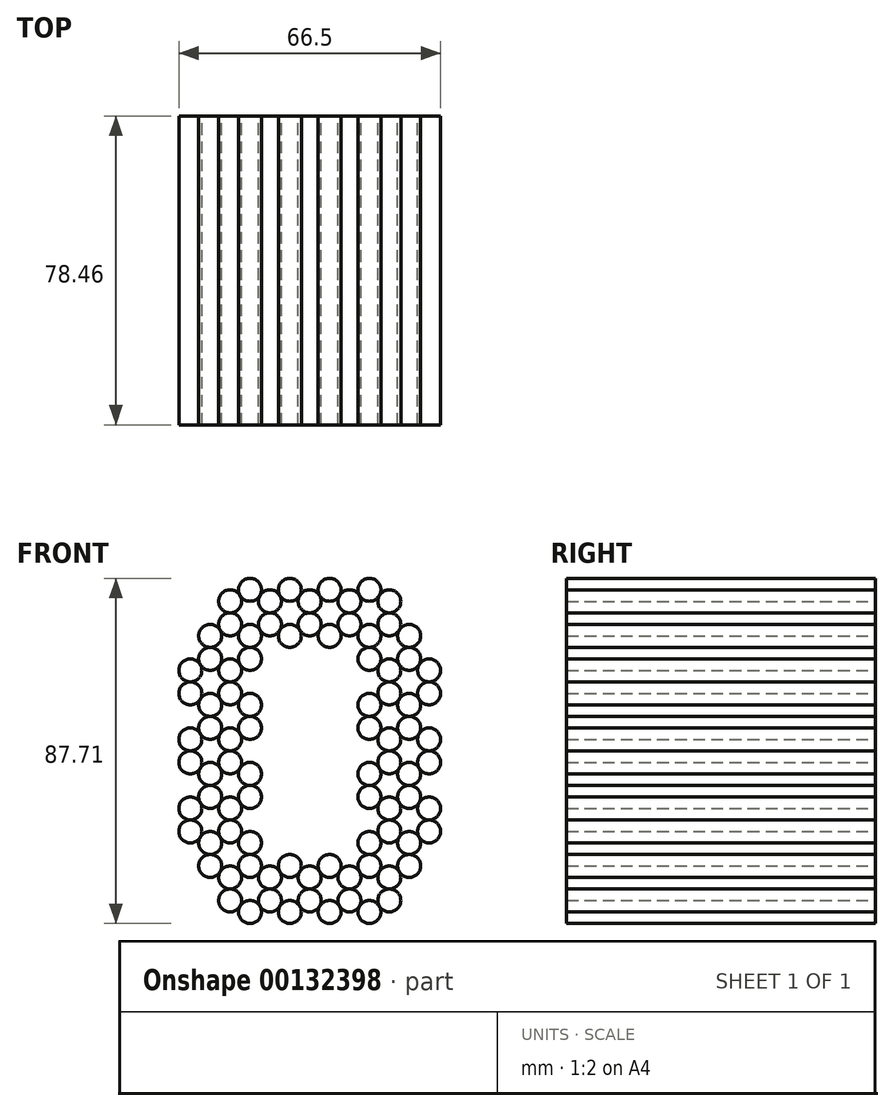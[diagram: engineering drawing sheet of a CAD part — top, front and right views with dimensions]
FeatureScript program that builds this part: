
annotation { "Feature Type Name" : "Feature", "Feature Type Description" : "" }
export const myFeature = defineFeature(function(context is Context, id is Id, definition is map)
    precondition{}
    {
        {
            var Q0;
            Q0=qCreatedBy(makeId("Front.planeOp"),FACE);
            var sketch = newSketch(context, id + "F0", { "sketchPlane" : qUnion([Q0])});
            skCircle(sketch, "E0", {"center": v(0, 0) * mm, "radius": 2.92 * mm});
            skCircle(sketch, "E1", {"center": v(5.05, 8.77) * mm, "radius": 2.92 * mm});
            skCircle(sketch, "E2", {"center": v(5.05, -2.93) * mm, "radius": 2.92 * mm});
            skCircle(sketch, "E3", {"center": v(10.1, 0) * mm, "radius": 2.92 * mm});
            skCircle(sketch, "E4", {"center": v(15.16, -2.93) * mm, "radius": 2.92 * mm});
            skCircle(sketch, "E5", {"center": v(10.1, 5.84) * mm, "radius": 2.92 * mm});
            skCircle(sketch, "E6", {"center": v(20.22, 0) * mm, "radius": 2.92 * mm});
            skCircle(sketch, "E7", {"center": v(20.22, 5.84) * mm, "radius": 2.92 * mm});
            skCircle(sketch, "E8", {"center": v(15.16, 8.77) * mm, "radius": 2.92 * mm});
            skCircle(sketch, "E9", {"center": v(-5.05, -2.93) * mm, "radius": 2.92 * mm});
            skCircle(sketch, "E10", {"center": v(0, 5.84) * mm, "radius": 2.92 * mm});
            skCircle(sketch, "E11", {"center": v(-5.05, 8.77) * mm, "radius": 2.92 * mm});
            skCircle(sketch, "E12", {"center": v(-10.1, 0) * mm, "radius": 2.92 * mm});
            skCircle(sketch, "E13", {"center": v(-15.16, 8.77) * mm, "radius": 2.92 * mm});
            skCircle(sketch, "E14", {"center": v(-10.1, 5.84) * mm, "radius": 2.92 * mm});
            skCircle(sketch, "E15", {"center": v(-20.22, 5.84) * mm, "radius": 2.92 * mm});
            skCircle(sketch, "E16", {"center": v(-20.22, 0) * mm, "radius": 2.92 * mm});
            skCircle(sketch, "E17", {"center": v(-15.16, -2.93) * mm, "radius": 2.92 * mm});
            skCircle(sketch, "E18", {"center": v(-25.27, -2.93) * mm, "radius": 2.92 * mm});
            skCircle(sketch, "E19", {"center": v(-25.27, -8.77) * mm, "radius": 2.92 * mm});
            skCircle(sketch, "E20", {"center": v(-20.22, -11.7) * mm, "radius": 2.92 * mm});
            skCircle(sketch, "E21", {"center": v(-15.16, -8.77) * mm, "radius": 2.92 * mm});
            skCircle(sketch, "E22", {"center": v(-30.33, -11.7) * mm, "radius": 2.92 * mm});
            skCircle(sketch, "E23", {"center": v(-30.33, -17.54) * mm, "radius": 2.92 * mm});
            skCircle(sketch, "E24", {"center": v(-25.27, -20.47) * mm, "radius": 2.92 * mm});
            skCircle(sketch, "E25", {"center": v(-20.22, -17.54) * mm, "radius": 2.92 * mm});
            skCircle(sketch, "E26", {"center": v(-15.16, -20.47) * mm, "radius": 2.92 * mm});
            skCircle(sketch, "E27", {"center": v(-25.27, -26.31) * mm, "radius": 2.92 * mm});
            skCircle(sketch, "E28", {"center": v(-20.22, -29.24) * mm, "radius": 2.92 * mm});
            skCircle(sketch, "E29", {"center": v(-15.16, -26.31) * mm, "radius": 2.92 * mm});
            skCircle(sketch, "E30", {"center": v(-30.33, -29.24) * mm, "radius": 2.92 * mm});
            skCircle(sketch, "E31", {"center": v(-30.33, -35.08) * mm, "radius": 2.92 * mm});
            skCircle(sketch, "E32", {"center": v(-25.27, -38.01) * mm, "radius": 2.92 * mm});
            skCircle(sketch, "E33", {"center": v(-20.22, -35.08) * mm, "radius": 2.92 * mm});
            skCircle(sketch, "E34", {"center": v(-15.16, -38.01) * mm, "radius": 2.92 * mm});
            skCircle(sketch, "E35", {"center": v(-25.27, -43.86) * mm, "radius": 2.92 * mm});
            skCircle(sketch, "E36", {"center": v(-20.22, -46.78) * mm, "radius": 2.92 * mm});
            skCircle(sketch, "E37", {"center": v(-15.16, -43.86) * mm, "radius": 2.92 * mm});
            skCircle(sketch, "E38", {"center": v(-30.33, -46.78) * mm, "radius": 2.92 * mm});
            skCircle(sketch, "E39", {"center": v(-30.33, -52.63) * mm, "radius": 2.92 * mm});
            skCircle(sketch, "E40", {"center": v(-25.27, -55.56) * mm, "radius": 2.92 * mm});
            skCircle(sketch, "E41", {"center": v(-20.22, -52.63) * mm, "radius": 2.92 * mm});
            skCircle(sketch, "E42", {"center": v(-15.16, -55.56) * mm, "radius": 2.92 * mm});
            skCircle(sketch, "E43", {"center": v(-25.27, -61.4) * mm, "radius": 2.92 * mm});
            skCircle(sketch, "E44", {"center": v(-20.22, -64.33) * mm, "radius": 2.92 * mm});
            skCircle(sketch, "E45", {"center": v(-15.16, -61.4) * mm, "radius": 2.92 * mm});
            skCircle(sketch, "E46", {"center": v(0, -70.17) * mm, "radius": 2.92 * mm});
            skCircle(sketch, "E47", {"center": v(5.05, -61.4) * mm, "radius": 2.92 * mm});
            skCircle(sketch, "E48", {"center": v(5.05, -73.1) * mm, "radius": 2.92 * mm});
            skCircle(sketch, "E49", {"center": v(10.1, -70.17) * mm, "radius": 2.92 * mm});
            skCircle(sketch, "E50", {"center": v(15.16, -73.1) * mm, "radius": 2.92 * mm});
            skCircle(sketch, "E51", {"center": v(10.1, -64.33) * mm, "radius": 2.92 * mm});
            skCircle(sketch, "E52", {"center": v(20.22, -70.17) * mm, "radius": 2.92 * mm});
            skCircle(sketch, "E53", {"center": v(20.22, -64.33) * mm, "radius": 2.92 * mm});
            skCircle(sketch, "E54", {"center": v(15.16, -61.4) * mm, "radius": 2.92 * mm});
            skCircle(sketch, "E55", {"center": v(-5.05, -73.1) * mm, "radius": 2.92 * mm});
            skCircle(sketch, "E56", {"center": v(0, -64.33) * mm, "radius": 2.92 * mm});
            skCircle(sketch, "E57", {"center": v(-5.05, -61.4) * mm, "radius": 2.92 * mm});
            skCircle(sketch, "E58", {"center": v(-10.1, -70.17) * mm, "radius": 2.92 * mm});
            skCircle(sketch, "E59", {"center": v(-10.1, -64.33) * mm, "radius": 2.92 * mm});
            skCircle(sketch, "E60", {"center": v(-20.22, -70.17) * mm, "radius": 2.92 * mm});
            skCircle(sketch, "E61", {"center": v(-15.16, -73.1) * mm, "radius": 2.92 * mm});
            skCircle(sketch, "E62", {"center": v(25.27, -20.47) * mm, "radius": 2.92 * mm});
            skCircle(sketch, "E63", {"center": v(15.16, -20.47) * mm, "radius": 2.92 * mm});
            skCircle(sketch, "E64", {"center": v(15.16, -26.31) * mm, "radius": 2.92 * mm});
            skCircle(sketch, "E65", {"center": v(20.22, -29.24) * mm, "radius": 2.92 * mm});
            skCircle(sketch, "E66", {"center": v(25.27, -26.31) * mm, "radius": 2.92 * mm});
            skCircle(sketch, "E67", {"center": v(30.33, -29.24) * mm, "radius": 2.92 * mm});
            skCircle(sketch, "E68", {"center": v(20.22, -35.08) * mm, "radius": 2.92 * mm});
            skCircle(sketch, "E69", {"center": v(25.27, -38.01) * mm, "radius": 2.92 * mm});
            skCircle(sketch, "E70", {"center": v(30.33, -35.08) * mm, "radius": 2.92 * mm});
            skCircle(sketch, "E71", {"center": v(15.16, -38.01) * mm, "radius": 2.92 * mm});
            skCircle(sketch, "E72", {"center": v(15.16, -43.86) * mm, "radius": 2.92 * mm});
            skCircle(sketch, "E73", {"center": v(20.22, -46.78) * mm, "radius": 2.92 * mm});
            skCircle(sketch, "E74", {"center": v(25.27, -43.86) * mm, "radius": 2.92 * mm});
            skCircle(sketch, "E75", {"center": v(30.33, -46.78) * mm, "radius": 2.92 * mm});
            skCircle(sketch, "E76", {"center": v(20.22, -52.63) * mm, "radius": 2.92 * mm});
            skCircle(sketch, "E77", {"center": v(25.27, -55.56) * mm, "radius": 2.92 * mm});
            skCircle(sketch, "E78", {"center": v(30.33, -52.63) * mm, "radius": 2.92 * mm});
            skCircle(sketch, "E79", {"center": v(15.16, -55.56) * mm, "radius": 2.92 * mm});
            skCircle(sketch, "E80", {"center": v(25.27, -61.4) * mm, "radius": 2.92 * mm});
            skCircle(sketch, "E81", {"center": v(15.16, -8.77) * mm, "radius": 2.92 * mm});
            skCircle(sketch, "E82", {"center": v(20.22, -17.54) * mm, "radius": 2.92 * mm});
            skCircle(sketch, "E83", {"center": v(20.22, -11.7) * mm, "radius": 2.92 * mm});
            skCircle(sketch, "E84", {"center": v(25.27, -2.93) * mm, "radius": 2.92 * mm});
            skCircle(sketch, "E85", {"center": v(25.27, -8.77) * mm, "radius": 2.92 * mm});
            skCircle(sketch, "E86", {"center": v(30.33, -17.54) * mm, "radius": 2.92 * mm});
            skCircle(sketch, "E87", {"center": v(30.33, -11.7) * mm, "radius": 2.92 * mm});
            skSolve(sketch);
        }
        {
            var Q0;
            {var subQ0=sQuery(id+"F0.wireOp",EDGE,"E69");var subQ1=makeQuery(id+"F0.imprint","INTERSECT",VERTEX,{"derivedFrom":[subQ0,sQuery(id+"F0.wireOp",EDGE,"E70")]});Q0=makeQuery(id+"F0.imprint","IMPRINT",FACE,{"disambiguationData":[TD([[makeQuery(id+"F0.imprint","IMPRINT",EDGE,{"disambiguationData":[TD([[subQ1,-1.0]])],"derivedFrom":subQ0}),1.0]])]});}
            var Q1;
            {var subQ0=sQuery(id+"F0.wireOp",EDGE,"E34");var subQ1=makeQuery(id+"F0.imprint","INTERSECT",VERTEX,{"derivedFrom":[sQuery(id+"F0.wireOp",EDGE,"E33"),subQ0]});Q1=makeQuery(id+"F0.imprint","IMPRINT",FACE,{"disambiguationData":[TD([[makeQuery(id+"F0.imprint","IMPRINT",EDGE,{"disambiguationData":[TD([[subQ1,-1.0]])],"derivedFrom":subQ0}),1.0]])]});}
            var Q2;
            {var subQ0=sQuery(id+"F0.wireOp",EDGE,"E86");var subQ1=makeQuery(id+"F0.imprint","INTERSECT",VERTEX,{"derivedFrom":[sQuery(id+"F0.wireOp",EDGE,"E62"),subQ0]});Q2=makeQuery(id+"F0.imprint","IMPRINT",FACE,{"disambiguationData":[TD([[makeQuery(id+"F0.imprint","IMPRINT",EDGE,{"disambiguationData":[TD([[subQ1,1.0]])],"derivedFrom":subQ0}),1.0]])]});}
            var Q3;
            {var subQ0=sQuery(id+"F0.wireOp",EDGE,"E33");var subQ1=makeQuery(id+"F0.imprint","INTERSECT",VERTEX,{"derivedFrom":[sQuery(id+"F0.wireOp",EDGE,"E28"),subQ0]});Q3=makeQuery(id+"F0.imprint","IMPRINT",FACE,{"disambiguationData":[TD([[makeQuery(id+"F0.imprint","IMPRINT",EDGE,{"disambiguationData":[TD([[subQ1,-1.0]])],"derivedFrom":subQ0}),1.0]])]});}
            var Q4;
            {var subQ0=sQuery(id+"F0.wireOp",EDGE,"E45");var subQ1=makeQuery(id+"F0.imprint","INTERSECT",VERTEX,{"derivedFrom":[sQuery(id+"F0.wireOp",EDGE,"E42"),subQ0]});Q4=makeQuery(id+"F0.imprint","IMPRINT",FACE,{"disambiguationData":[TD([[makeQuery(id+"F0.imprint","IMPRINT",EDGE,{"disambiguationData":[TD([[subQ1,-1.0]])],"derivedFrom":subQ0}),1.0]])]});}
            var Q5;
            {var subQ0=sQuery(id+"F0.wireOp",EDGE,"E74");var subQ1=makeQuery(id+"F0.imprint","INTERSECT",VERTEX,{"derivedFrom":[sQuery(id+"F0.wireOp",EDGE,"E69"),subQ0]});Q5=makeQuery(id+"F0.imprint","IMPRINT",FACE,{"disambiguationData":[TD([[makeQuery(id+"F0.imprint","IMPRINT",EDGE,{"disambiguationData":[TD([[subQ1,-1.0]])],"derivedFrom":subQ0}),1.0]])]});}
            var Q6;
            {var subQ0=sQuery(id+"F0.wireOp",EDGE,"E40");var subQ1=makeQuery(id+"F0.imprint","INTERSECT",VERTEX,{"derivedFrom":[sQuery(id+"F0.wireOp",EDGE,"E39"),subQ0]});Q6=makeQuery(id+"F0.imprint","IMPRINT",FACE,{"disambiguationData":[TD([[makeQuery(id+"F0.imprint","IMPRINT",EDGE,{"disambiguationData":[TD([[subQ1,1.0]])],"derivedFrom":subQ0}),1.0]])]});}
            var Q7;
            {var subQ0=sQuery(id+"F0.wireOp",EDGE,"E5");var subQ1=makeQuery(id+"F0.imprint","INTERSECT",VERTEX,{"derivedFrom":[sQuery(id+"F0.wireOp",EDGE,"E1"),subQ0]});Q7=makeQuery(id+"F0.imprint","IMPRINT",FACE,{"disambiguationData":[TD([[makeQuery(id+"F0.imprint","IMPRINT",EDGE,{"disambiguationData":[TD([[subQ1,1.0]])],"derivedFrom":subQ0}),1.0]])]});}
            var Q8;
            {var subQ0=sQuery(id+"F0.wireOp",EDGE,"E71");var subQ1=makeQuery(id+"F0.imprint","INTERSECT",VERTEX,{"derivedFrom":[sQuery(id+"F0.wireOp",EDGE,"E68"),subQ0]});Q8=makeQuery(id+"F0.imprint","IMPRINT",FACE,{"disambiguationData":[TD([[makeQuery(id+"F0.imprint","IMPRINT",EDGE,{"disambiguationData":[TD([[subQ1,-1.0]])],"derivedFrom":subQ0}),1.0]])]});}
            var Q9;
            {var subQ0=sQuery(id+"F0.wireOp",EDGE,"E35");var subQ1=makeQuery(id+"F0.imprint","INTERSECT",VERTEX,{"derivedFrom":[sQuery(id+"F0.wireOp",EDGE,"E32"),subQ0]});Q9=makeQuery(id+"F0.imprint","IMPRINT",FACE,{"disambiguationData":[TD([[makeQuery(id+"F0.imprint","IMPRINT",EDGE,{"disambiguationData":[TD([[subQ1,-1.0]])],"derivedFrom":subQ0}),1.0]])]});}
            var Q10;
            {var subQ0=sQuery(id+"F0.wireOp",EDGE,"E87");var subQ1=makeQuery(id+"F0.imprint","INTERSECT",VERTEX,{"derivedFrom":[sQuery(id+"F0.wireOp",EDGE,"E85"),subQ0]});Q10=makeQuery(id+"F0.imprint","IMPRINT",FACE,{"disambiguationData":[TD([[makeQuery(id+"F0.imprint","IMPRINT",EDGE,{"disambiguationData":[TD([[subQ1,-1.0]])],"derivedFrom":subQ0}),1.0]])]});}
            var Q11;
            {var subQ0=sQuery(id+"F0.wireOp",EDGE,"E36");var subQ1=makeQuery(id+"F0.imprint","INTERSECT",VERTEX,{"derivedFrom":[sQuery(id+"F0.wireOp",EDGE,"E35"),subQ0]});Q11=makeQuery(id+"F0.imprint","IMPRINT",FACE,{"disambiguationData":[TD([[makeQuery(id+"F0.imprint","IMPRINT",EDGE,{"disambiguationData":[TD([[subQ1,1.0]])],"derivedFrom":subQ0}),1.0]])]});}
            var Q12;
            {var subQ0=sQuery(id+"F0.wireOp",EDGE,"E51");var subQ1=makeQuery(id+"F0.imprint","INTERSECT",VERTEX,{"derivedFrom":[sQuery(id+"F0.wireOp",EDGE,"E47"),subQ0]});Q12=makeQuery(id+"F0.imprint","IMPRINT",FACE,{"disambiguationData":[TD([[makeQuery(id+"F0.imprint","IMPRINT",EDGE,{"disambiguationData":[TD([[subQ1,1.0]])],"derivedFrom":subQ0}),1.0]])]});}
            var Q13;
            {var subQ0=sQuery(id+"F0.wireOp",EDGE,"E77");var subQ1=makeQuery(id+"F0.imprint","INTERSECT",VERTEX,{"derivedFrom":[subQ0,sQuery(id+"F0.wireOp",EDGE,"E78")]});Q13=makeQuery(id+"F0.imprint","IMPRINT",FACE,{"disambiguationData":[TD([[makeQuery(id+"F0.imprint","IMPRINT",EDGE,{"disambiguationData":[TD([[subQ1,-1.0]])],"derivedFrom":subQ0}),1.0]])]});}
            var Q14;
            {var subQ0=sQuery(id+"F0.wireOp",EDGE,"E42");var subQ1=makeQuery(id+"F0.imprint","INTERSECT",VERTEX,{"derivedFrom":[sQuery(id+"F0.wireOp",EDGE,"E41"),subQ0]});Q14=makeQuery(id+"F0.imprint","IMPRINT",FACE,{"disambiguationData":[TD([[makeQuery(id+"F0.imprint","IMPRINT",EDGE,{"disambiguationData":[TD([[subQ1,-1.0]])],"derivedFrom":subQ0}),1.0]])]});}
            var Q15;
            {var subQ0=sQuery(id+"F0.wireOp",EDGE,"E6");var subQ1=makeQuery(id+"F0.imprint","INTERSECT",VERTEX,{"derivedFrom":[subQ0,sQuery(id+"F0.wireOp",EDGE,"E7")]});Q15=makeQuery(id+"F0.imprint","IMPRINT",FACE,{"disambiguationData":[TD([[makeQuery(id+"F0.imprint","IMPRINT",EDGE,{"disambiguationData":[TD([[subQ1,-1.0]])],"derivedFrom":subQ0}),1.0]])]});}
            var Q16;
            {var subQ0=sQuery(id+"F0.wireOp",EDGE,"E72");var subQ1=makeQuery(id+"F0.imprint","INTERSECT",VERTEX,{"derivedFrom":[sQuery(id+"F0.wireOp",EDGE,"E71"),subQ0]});Q16=makeQuery(id+"F0.imprint","IMPRINT",FACE,{"disambiguationData":[TD([[makeQuery(id+"F0.imprint","IMPRINT",EDGE,{"disambiguationData":[TD([[subQ1,-1.0]])],"derivedFrom":subQ0}),1.0]])]});}
            var Q17;
            {var subQ0=sQuery(id+"F0.wireOp",EDGE,"E37");var subQ1=makeQuery(id+"F0.imprint","INTERSECT",VERTEX,{"derivedFrom":[sQuery(id+"F0.wireOp",EDGE,"E34"),subQ0]});Q17=makeQuery(id+"F0.imprint","IMPRINT",FACE,{"disambiguationData":[TD([[makeQuery(id+"F0.imprint","IMPRINT",EDGE,{"disambiguationData":[TD([[subQ1,-1.0]])],"derivedFrom":subQ0}),1.0]])]});}
            var Q18;
            {var subQ0=sQuery(id+"F0.wireOp",EDGE,"E2");var subQ1=makeQuery(id+"F0.imprint","INTERSECT",VERTEX,{"derivedFrom":[sQuery(id+"F0.wireOp",EDGE,"E0"),subQ0]});Q18=makeQuery(id+"F0.imprint","IMPRINT",FACE,{"disambiguationData":[TD([[makeQuery(id+"F0.imprint","IMPRINT",EDGE,{"disambiguationData":[TD([[subQ1,1.0]])],"derivedFrom":subQ0}),1.0]])]});}
            var Q19;
            {var subQ0=sQuery(id+"F0.wireOp",EDGE,"E41");var subQ1=makeQuery(id+"F0.imprint","INTERSECT",VERTEX,{"derivedFrom":[sQuery(id+"F0.wireOp",EDGE,"E36"),subQ0]});Q19=makeQuery(id+"F0.imprint","IMPRINT",FACE,{"disambiguationData":[TD([[makeQuery(id+"F0.imprint","IMPRINT",EDGE,{"disambiguationData":[TD([[subQ1,-1.0]])],"derivedFrom":subQ0}),1.0]])]});}
            var Q20;
            {var subQ0=sQuery(id+"F0.wireOp",EDGE,"E52");var subQ1=makeQuery(id+"F0.imprint","INTERSECT",VERTEX,{"derivedFrom":[sQuery(id+"F0.wireOp",EDGE,"E50"),subQ0]});Q20=makeQuery(id+"F0.imprint","IMPRINT",FACE,{"disambiguationData":[TD([[makeQuery(id+"F0.imprint","IMPRINT",EDGE,{"disambiguationData":[TD([[subQ1,1.0]])],"derivedFrom":subQ0}),1.0]])]});}
            var Q21;
            {var subQ0=sQuery(id+"F0.wireOp",EDGE,"E56");var subQ1=makeQuery(id+"F0.imprint","INTERSECT",VERTEX,{"derivedFrom":[sQuery(id+"F0.wireOp",EDGE,"E46"),subQ0]});Q21=makeQuery(id+"F0.imprint","IMPRINT",FACE,{"disambiguationData":[TD([[makeQuery(id+"F0.imprint","IMPRINT",EDGE,{"disambiguationData":[TD([[subQ1,1.0]])],"derivedFrom":subQ0}),1.0]])]});}
            var Q22;
            {var subQ0=sQuery(id+"F0.wireOp",EDGE,"E81");var subQ1=makeQuery(id+"F0.imprint","INTERSECT",VERTEX,{"derivedFrom":[sQuery(id+"F0.wireOp",EDGE,"E4"),subQ0]});Q22=makeQuery(id+"F0.imprint","IMPRINT",FACE,{"disambiguationData":[TD([[makeQuery(id+"F0.imprint","IMPRINT",EDGE,{"disambiguationData":[TD([[subQ1,-1.0]])],"derivedFrom":subQ0}),1.0]])]});}
            var Q23;
            {var subQ0=sQuery(id+"F0.wireOp",EDGE,"E46");var subQ1=makeQuery(id+"F0.imprint","INTERSECT",VERTEX,{"derivedFrom":[subQ0,sQuery(id+"F0.wireOp",EDGE,"E55")]});Q23=makeQuery(id+"F0.imprint","IMPRINT",FACE,{"disambiguationData":[TD([[makeQuery(id+"F0.imprint","IMPRINT",EDGE,{"disambiguationData":[TD([[subQ1,1.0]])],"derivedFrom":subQ0}),1.0]])]});}
            var Q24;
            {var subQ0=sQuery(id+"F0.wireOp",EDGE,"E10");var subQ1=makeQuery(id+"F0.imprint","INTERSECT",VERTEX,{"derivedFrom":[subQ0,sQuery(id+"F0.wireOp",EDGE,"E11")]});Q24=makeQuery(id+"F0.imprint","IMPRINT",FACE,{"disambiguationData":[TD([[makeQuery(id+"F0.imprint","IMPRINT",EDGE,{"disambiguationData":[TD([[subQ1,-1.0]])],"derivedFrom":subQ0}),1.0]])]});}
            var Q25;
            {var subQ0=sQuery(id+"F0.wireOp",EDGE,"E55");var subQ1=makeQuery(id+"F0.imprint","INTERSECT",VERTEX,{"derivedFrom":[sQuery(id+"F0.wireOp",EDGE,"E46"),subQ0]});Q25=makeQuery(id+"F0.imprint","IMPRINT",FACE,{"disambiguationData":[TD([[makeQuery(id+"F0.imprint","IMPRINT",EDGE,{"disambiguationData":[TD([[subQ1,-1.0]])],"derivedFrom":subQ0}),1.0]])]});}
            var Q26;
            {var subQ0=sQuery(id+"F0.wireOp",EDGE,"E59");var subQ1=makeQuery(id+"F0.imprint","INTERSECT",VERTEX,{"derivedFrom":[sQuery(id+"F0.wireOp",EDGE,"E45"),subQ0]});Q26=makeQuery(id+"F0.imprint","IMPRINT",FACE,{"disambiguationData":[TD([[makeQuery(id+"F0.imprint","IMPRINT",EDGE,{"disambiguationData":[TD([[subQ1,1.0]])],"derivedFrom":subQ0}),1.0]])]});}
            var Q27;
            {var subQ0=sQuery(id+"F0.wireOp",EDGE,"E85");var subQ1=makeQuery(id+"F0.imprint","INTERSECT",VERTEX,{"derivedFrom":[sQuery(id+"F0.wireOp",EDGE,"E84"),subQ0]});Q27=makeQuery(id+"F0.imprint","IMPRINT",FACE,{"disambiguationData":[TD([[makeQuery(id+"F0.imprint","IMPRINT",EDGE,{"disambiguationData":[TD([[subQ1,-1.0]])],"derivedFrom":subQ0}),1.0]])]});}
            var Q28;
            {var subQ0=sQuery(id+"F0.wireOp",EDGE,"E47");var subQ1=makeQuery(id+"F0.imprint","INTERSECT",VERTEX,{"derivedFrom":[subQ0,sQuery(id+"F0.wireOp",EDGE,"E51")]});Q28=makeQuery(id+"F0.imprint","IMPRINT",FACE,{"disambiguationData":[TD([[makeQuery(id+"F0.imprint","IMPRINT",EDGE,{"disambiguationData":[TD([[subQ1,1.0]])],"derivedFrom":subQ0}),1.0]])]});}
            var Q29;
            {var subQ0=sQuery(id+"F0.wireOp",EDGE,"E14");var subQ1=makeQuery(id+"F0.imprint","INTERSECT",VERTEX,{"derivedFrom":[sQuery(id+"F0.wireOp",EDGE,"E11"),subQ0]});Q29=makeQuery(id+"F0.imprint","IMPRINT",FACE,{"disambiguationData":[TD([[makeQuery(id+"F0.imprint","IMPRINT",EDGE,{"disambiguationData":[TD([[subQ1,-1.0]])],"derivedFrom":subQ0}),1.0]])]});}
            var Q30;
            {var subQ0=sQuery(id+"F0.wireOp",EDGE,"E60");var subQ1=makeQuery(id+"F0.imprint","INTERSECT",VERTEX,{"derivedFrom":[sQuery(id+"F0.wireOp",EDGE,"E44"),subQ0]});Q30=makeQuery(id+"F0.imprint","IMPRINT",FACE,{"disambiguationData":[TD([[makeQuery(id+"F0.imprint","IMPRINT",EDGE,{"disambiguationData":[TD([[subQ1,-1.0]])],"derivedFrom":subQ0}),1.0]])]});}
            var Q31;
            {var subQ0=sQuery(id+"F0.wireOp",EDGE,"E65");var subQ1=makeQuery(id+"F0.imprint","INTERSECT",VERTEX,{"derivedFrom":[sQuery(id+"F0.wireOp",EDGE,"E64"),subQ0]});Q31=makeQuery(id+"F0.imprint","IMPRINT",FACE,{"disambiguationData":[TD([[makeQuery(id+"F0.imprint","IMPRINT",EDGE,{"disambiguationData":[TD([[subQ1,1.0]])],"derivedFrom":subQ0}),1.0]])]});}
            var Q32;
            {var subQ0=sQuery(id+"F0.wireOp",EDGE,"E0");var subQ1=makeQuery(id+"F0.imprint","INTERSECT",VERTEX,{"derivedFrom":[subQ0,sQuery(id+"F0.wireOp",EDGE,"E9")]});Q32=makeQuery(id+"F0.imprint","IMPRINT",FACE,{"disambiguationData":[TD([[makeQuery(id+"F0.imprint","IMPRINT",EDGE,{"disambiguationData":[TD([[subQ1,1.0]])],"derivedFrom":subQ0}),1.0]])]});}
            var Q33;
            {var subQ0=sQuery(id+"F0.wireOp",EDGE,"E49");var subQ1=makeQuery(id+"F0.imprint","INTERSECT",VERTEX,{"derivedFrom":[sQuery(id+"F0.wireOp",EDGE,"E48"),subQ0]});Q33=makeQuery(id+"F0.imprint","IMPRINT",FACE,{"disambiguationData":[TD([[makeQuery(id+"F0.imprint","IMPRINT",EDGE,{"disambiguationData":[TD([[subQ1,1.0]])],"derivedFrom":subQ0}),1.0]])]});}
            var Q34;
            {var subQ0=sQuery(id+"F0.wireOp",EDGE,"E16");var subQ1=makeQuery(id+"F0.imprint","INTERSECT",VERTEX,{"derivedFrom":[sQuery(id+"F0.wireOp",EDGE,"E15"),subQ0]});Q34=makeQuery(id+"F0.imprint","IMPRINT",FACE,{"disambiguationData":[TD([[makeQuery(id+"F0.imprint","IMPRINT",EDGE,{"disambiguationData":[TD([[subQ1,-1.0]])],"derivedFrom":subQ0}),1.0]])]});}
            var Q35;
            {var subQ0=sQuery(id+"F0.wireOp",EDGE,"E61");var subQ1=makeQuery(id+"F0.imprint","INTERSECT",VERTEX,{"derivedFrom":[sQuery(id+"F0.wireOp",EDGE,"E58"),subQ0]});Q35=makeQuery(id+"F0.imprint","IMPRINT",FACE,{"disambiguationData":[TD([[makeQuery(id+"F0.imprint","IMPRINT",EDGE,{"disambiguationData":[TD([[subQ1,-1.0]])],"derivedFrom":subQ0}),1.0]])]});}
            var Q36;
            {var subQ0=sQuery(id+"F0.wireOp",EDGE,"E68");var subQ1=makeQuery(id+"F0.imprint","INTERSECT",VERTEX,{"derivedFrom":[sQuery(id+"F0.wireOp",EDGE,"E65"),subQ0]});Q36=makeQuery(id+"F0.imprint","IMPRINT",FACE,{"disambiguationData":[TD([[makeQuery(id+"F0.imprint","IMPRINT",EDGE,{"disambiguationData":[TD([[subQ1,-1.0]])],"derivedFrom":subQ0}),1.0]])]});}
            var Q37;
            {var subQ0=sQuery(id+"F0.wireOp",EDGE,"E3");var subQ1=makeQuery(id+"F0.imprint","INTERSECT",VERTEX,{"derivedFrom":[sQuery(id+"F0.wireOp",EDGE,"E2"),subQ0]});Q37=makeQuery(id+"F0.imprint","IMPRINT",FACE,{"disambiguationData":[TD([[makeQuery(id+"F0.imprint","IMPRINT",EDGE,{"disambiguationData":[TD([[subQ1,1.0]])],"derivedFrom":subQ0}),1.0]])]});}
            var Q38;
            {var subQ0=sQuery(id+"F0.wireOp",EDGE,"E53");var subQ1=makeQuery(id+"F0.imprint","INTERSECT",VERTEX,{"derivedFrom":[subQ0,sQuery(id+"F0.wireOp",EDGE,"E80")]});Q38=makeQuery(id+"F0.imprint","IMPRINT",FACE,{"disambiguationData":[TD([[makeQuery(id+"F0.imprint","IMPRINT",EDGE,{"disambiguationData":[TD([[subQ1,-1.0]])],"derivedFrom":subQ0}),1.0]])]});}
            var Q39;
            {var subQ0=sQuery(id+"F0.wireOp",EDGE,"E19");var subQ1=makeQuery(id+"F0.imprint","INTERSECT",VERTEX,{"derivedFrom":[sQuery(id+"F0.wireOp",EDGE,"E18"),subQ0]});Q39=makeQuery(id+"F0.imprint","IMPRINT",FACE,{"disambiguationData":[TD([[makeQuery(id+"F0.imprint","IMPRINT",EDGE,{"disambiguationData":[TD([[subQ1,-1.0]])],"derivedFrom":subQ0}),1.0]])]});}
            var Q40;
            {var subQ0=sQuery(id+"F0.wireOp",EDGE,"E67");var subQ1=makeQuery(id+"F0.imprint","INTERSECT",VERTEX,{"derivedFrom":[sQuery(id+"F0.wireOp",EDGE,"E66"),subQ0]});Q40=makeQuery(id+"F0.imprint","IMPRINT",FACE,{"disambiguationData":[TD([[makeQuery(id+"F0.imprint","IMPRINT",EDGE,{"disambiguationData":[TD([[subQ1,-1.0]])],"derivedFrom":subQ0}),1.0]])]});}
            var Q41;
            {var subQ0=sQuery(id+"F0.wireOp",EDGE,"E73");var subQ1=makeQuery(id+"F0.imprint","INTERSECT",VERTEX,{"derivedFrom":[sQuery(id+"F0.wireOp",EDGE,"E72"),subQ0]});Q41=makeQuery(id+"F0.imprint","IMPRINT",FACE,{"disambiguationData":[TD([[makeQuery(id+"F0.imprint","IMPRINT",EDGE,{"disambiguationData":[TD([[subQ1,1.0]])],"derivedFrom":subQ0}),1.0]])]});}
            var Q42;
            {var subQ0=sQuery(id+"F0.wireOp",EDGE,"E4");var subQ1=makeQuery(id+"F0.imprint","INTERSECT",VERTEX,{"derivedFrom":[sQuery(id+"F0.wireOp",EDGE,"E3"),subQ0]});Q42=makeQuery(id+"F0.imprint","IMPRINT",FACE,{"disambiguationData":[TD([[makeQuery(id+"F0.imprint","IMPRINT",EDGE,{"disambiguationData":[TD([[subQ1,1.0]])],"derivedFrom":subQ0}),1.0]])]});}
            var Q43;
            {var subQ0=sQuery(id+"F0.wireOp",EDGE,"E57");var subQ1=makeQuery(id+"F0.imprint","INTERSECT",VERTEX,{"derivedFrom":[sQuery(id+"F0.wireOp",EDGE,"E56"),subQ0]});Q43=makeQuery(id+"F0.imprint","IMPRINT",FACE,{"disambiguationData":[TD([[makeQuery(id+"F0.imprint","IMPRINT",EDGE,{"disambiguationData":[TD([[subQ1,1.0]])],"derivedFrom":subQ0}),1.0]])]});}
            var Q44;
            {var subQ0=sQuery(id+"F0.wireOp",EDGE,"E21");var subQ1=makeQuery(id+"F0.imprint","INTERSECT",VERTEX,{"derivedFrom":[sQuery(id+"F0.wireOp",EDGE,"E17"),subQ0]});Q44=makeQuery(id+"F0.imprint","IMPRINT",FACE,{"disambiguationData":[TD([[makeQuery(id+"F0.imprint","IMPRINT",EDGE,{"disambiguationData":[TD([[subQ1,-1.0]])],"derivedFrom":subQ0}),1.0]])]});}
            var Q45;
            {var subQ0=sQuery(id+"F0.wireOp",EDGE,"E70");var subQ1=makeQuery(id+"F0.imprint","INTERSECT",VERTEX,{"derivedFrom":[sQuery(id+"F0.wireOp",EDGE,"E67"),subQ0]});Q45=makeQuery(id+"F0.imprint","IMPRINT",FACE,{"disambiguationData":[TD([[makeQuery(id+"F0.imprint","IMPRINT",EDGE,{"disambiguationData":[TD([[subQ1,-1.0]])],"derivedFrom":subQ0}),1.0]])]});}
            var Q46;
            {var subQ0=sQuery(id+"F0.wireOp",EDGE,"E76");var subQ1=makeQuery(id+"F0.imprint","INTERSECT",VERTEX,{"derivedFrom":[sQuery(id+"F0.wireOp",EDGE,"E73"),subQ0]});Q46=makeQuery(id+"F0.imprint","IMPRINT",FACE,{"disambiguationData":[TD([[makeQuery(id+"F0.imprint","IMPRINT",EDGE,{"disambiguationData":[TD([[subQ1,-1.0]])],"derivedFrom":subQ0}),1.0]])]});}
            var Q47;
            {var subQ0=sQuery(id+"F0.wireOp",EDGE,"E12");var subQ1=makeQuery(id+"F0.imprint","INTERSECT",VERTEX,{"derivedFrom":[subQ0,sQuery(id+"F0.wireOp",EDGE,"E17")]});Q47=makeQuery(id+"F0.imprint","IMPRINT",FACE,{"disambiguationData":[TD([[makeQuery(id+"F0.imprint","IMPRINT",EDGE,{"disambiguationData":[TD([[subQ1,1.0]])],"derivedFrom":subQ0}),1.0]])]});}
            var Q48;
            {var subQ0=sQuery(id+"F0.wireOp",EDGE,"E58");var subQ1=makeQuery(id+"F0.imprint","INTERSECT",VERTEX,{"derivedFrom":[subQ0,sQuery(id+"F0.wireOp",EDGE,"E61")]});Q48=makeQuery(id+"F0.imprint","IMPRINT",FACE,{"disambiguationData":[TD([[makeQuery(id+"F0.imprint","IMPRINT",EDGE,{"disambiguationData":[TD([[subQ1,1.0]])],"derivedFrom":subQ0}),1.0]])]});}
            var Q49;
            {var subQ0=sQuery(id+"F0.wireOp",EDGE,"E24");var subQ1=makeQuery(id+"F0.imprint","INTERSECT",VERTEX,{"derivedFrom":[sQuery(id+"F0.wireOp",EDGE,"E23"),subQ0]});Q49=makeQuery(id+"F0.imprint","IMPRINT",FACE,{"disambiguationData":[TD([[makeQuery(id+"F0.imprint","IMPRINT",EDGE,{"disambiguationData":[TD([[subQ1,1.0]])],"derivedFrom":subQ0}),1.0]])]});}
            var Q50;
            {var subQ0=sQuery(id+"F0.wireOp",EDGE,"E82");var subQ1=makeQuery(id+"F0.imprint","INTERSECT",VERTEX,{"derivedFrom":[sQuery(id+"F0.wireOp",EDGE,"E63"),subQ0]});Q50=makeQuery(id+"F0.imprint","IMPRINT",FACE,{"disambiguationData":[TD([[makeQuery(id+"F0.imprint","IMPRINT",EDGE,{"disambiguationData":[TD([[subQ1,1.0]])],"derivedFrom":subQ0}),1.0]])]});}
            var Q51;
            {var subQ0=sQuery(id+"F0.wireOp",EDGE,"E17");var subQ1=makeQuery(id+"F0.imprint","INTERSECT",VERTEX,{"derivedFrom":[sQuery(id+"F0.wireOp",EDGE,"E12"),subQ0]});Q51=makeQuery(id+"F0.imprint","IMPRINT",FACE,{"disambiguationData":[TD([[makeQuery(id+"F0.imprint","IMPRINT",EDGE,{"disambiguationData":[TD([[subQ1,-1.0]])],"derivedFrom":subQ0}),1.0]])]});}
            var Q52;
            {var subQ0=sQuery(id+"F0.wireOp",EDGE,"E62");var subQ1=makeQuery(id+"F0.imprint","INTERSECT",VERTEX,{"derivedFrom":[subQ0,sQuery(id+"F0.wireOp",EDGE,"E86")]});Q52=makeQuery(id+"F0.imprint","IMPRINT",FACE,{"disambiguationData":[TD([[makeQuery(id+"F0.imprint","IMPRINT",EDGE,{"disambiguationData":[TD([[subQ1,-1.0]])],"derivedFrom":subQ0}),1.0]])]});}
            var Q53;
            {var subQ0=sQuery(id+"F0.wireOp",EDGE,"E26");var subQ1=makeQuery(id+"F0.imprint","INTERSECT",VERTEX,{"derivedFrom":[sQuery(id+"F0.wireOp",EDGE,"E25"),subQ0]});Q53=makeQuery(id+"F0.imprint","IMPRINT",FACE,{"disambiguationData":[TD([[makeQuery(id+"F0.imprint","IMPRINT",EDGE,{"disambiguationData":[TD([[subQ1,-1.0]])],"derivedFrom":subQ0}),1.0]])]});}
            var Q54;
            {var subQ0=sQuery(id+"F0.wireOp",EDGE,"E75");var subQ1=makeQuery(id+"F0.imprint","INTERSECT",VERTEX,{"derivedFrom":[sQuery(id+"F0.wireOp",EDGE,"E74"),subQ0]});Q54=makeQuery(id+"F0.imprint","IMPRINT",FACE,{"disambiguationData":[TD([[makeQuery(id+"F0.imprint","IMPRINT",EDGE,{"disambiguationData":[TD([[subQ1,-1.0]])],"derivedFrom":subQ0}),1.0]])]});}
            var Q55;
            {var subQ0=sQuery(id+"F0.wireOp",EDGE,"E50");var subQ1=makeQuery(id+"F0.imprint","INTERSECT",VERTEX,{"derivedFrom":[sQuery(id+"F0.wireOp",EDGE,"E49"),subQ0]});Q55=makeQuery(id+"F0.imprint","IMPRINT",FACE,{"disambiguationData":[TD([[makeQuery(id+"F0.imprint","IMPRINT",EDGE,{"disambiguationData":[TD([[subQ1,1.0]])],"derivedFrom":subQ0}),1.0]])]});}
            var Q56;
            {var subQ0=sQuery(id+"F0.wireOp",EDGE,"E43");var subQ1=makeQuery(id+"F0.imprint","INTERSECT",VERTEX,{"derivedFrom":[sQuery(id+"F0.wireOp",EDGE,"E40"),subQ0]});Q56=makeQuery(id+"F0.imprint","IMPRINT",FACE,{"disambiguationData":[TD([[makeQuery(id+"F0.imprint","IMPRINT",EDGE,{"disambiguationData":[TD([[subQ1,-1.0]])],"derivedFrom":subQ0}),1.0]])]});}
            var Q57;
            {var subQ0=sQuery(id+"F0.wireOp",EDGE,"E48");var subQ1=makeQuery(id+"F0.imprint","INTERSECT",VERTEX,{"derivedFrom":[sQuery(id+"F0.wireOp",EDGE,"E46"),subQ0]});Q57=makeQuery(id+"F0.imprint","IMPRINT",FACE,{"disambiguationData":[TD([[makeQuery(id+"F0.imprint","IMPRINT",EDGE,{"disambiguationData":[TD([[subQ1,1.0]])],"derivedFrom":subQ0}),1.0]])]});}
            var Q58;
            {var subQ0=sQuery(id+"F0.wireOp",EDGE,"E1");var subQ1=makeQuery(id+"F0.imprint","INTERSECT",VERTEX,{"derivedFrom":[subQ0,sQuery(id+"F0.wireOp",EDGE,"E5")]});Q58=makeQuery(id+"F0.imprint","IMPRINT",FACE,{"disambiguationData":[TD([[makeQuery(id+"F0.imprint","IMPRINT",EDGE,{"disambiguationData":[TD([[subQ1,1.0]])],"derivedFrom":subQ0}),1.0]])]});}
            var Q59;
            {var subQ0=sQuery(id+"F0.wireOp",EDGE,"E7");var subQ1=makeQuery(id+"F0.imprint","INTERSECT",VERTEX,{"derivedFrom":[sQuery(id+"F0.wireOp",EDGE,"E6"),subQ0]});Q59=makeQuery(id+"F0.imprint","IMPRINT",FACE,{"disambiguationData":[TD([[makeQuery(id+"F0.imprint","IMPRINT",EDGE,{"disambiguationData":[TD([[subQ1,1.0]])],"derivedFrom":subQ0}),1.0]])]});}
            var Q60;
            {var subQ0=sQuery(id+"F0.wireOp",EDGE,"E8");var subQ1=makeQuery(id+"F0.imprint","INTERSECT",VERTEX,{"derivedFrom":[sQuery(id+"F0.wireOp",EDGE,"E5"),subQ0]});Q60=makeQuery(id+"F0.imprint","IMPRINT",FACE,{"disambiguationData":[TD([[makeQuery(id+"F0.imprint","IMPRINT",EDGE,{"disambiguationData":[TD([[subQ1,-1.0]])],"derivedFrom":subQ0}),1.0]])]});}
            var Q61;
            {var subQ0=sQuery(id+"F0.wireOp",EDGE,"E11");var subQ1=makeQuery(id+"F0.imprint","INTERSECT",VERTEX,{"derivedFrom":[sQuery(id+"F0.wireOp",EDGE,"E10"),subQ0]});Q61=makeQuery(id+"F0.imprint","IMPRINT",FACE,{"disambiguationData":[TD([[makeQuery(id+"F0.imprint","IMPRINT",EDGE,{"disambiguationData":[TD([[subQ1,1.0]])],"derivedFrom":subQ0}),1.0]])]});}
            var Q62;
            {var subQ0=sQuery(id+"F0.wireOp",EDGE,"E13");var subQ1=makeQuery(id+"F0.imprint","INTERSECT",VERTEX,{"derivedFrom":[subQ0,sQuery(id+"F0.wireOp",EDGE,"E14")]});Q62=makeQuery(id+"F0.imprint","IMPRINT",FACE,{"disambiguationData":[TD([[makeQuery(id+"F0.imprint","IMPRINT",EDGE,{"disambiguationData":[TD([[subQ1,1.0]])],"derivedFrom":subQ0}),1.0]])]});}
            var Q63;
            {var subQ0=sQuery(id+"F0.wireOp",EDGE,"E15");var subQ1=makeQuery(id+"F0.imprint","INTERSECT",VERTEX,{"derivedFrom":[sQuery(id+"F0.wireOp",EDGE,"E13"),subQ0]});Q63=makeQuery(id+"F0.imprint","IMPRINT",FACE,{"disambiguationData":[TD([[makeQuery(id+"F0.imprint","IMPRINT",EDGE,{"disambiguationData":[TD([[subQ1,-1.0]])],"derivedFrom":subQ0}),1.0]])]});}
            var Q64;
            {var subQ0=sQuery(id+"F0.wireOp",EDGE,"E18");var subQ1=makeQuery(id+"F0.imprint","INTERSECT",VERTEX,{"derivedFrom":[sQuery(id+"F0.wireOp",EDGE,"E16"),subQ0]});Q64=makeQuery(id+"F0.imprint","IMPRINT",FACE,{"disambiguationData":[TD([[makeQuery(id+"F0.imprint","IMPRINT",EDGE,{"disambiguationData":[TD([[subQ1,-1.0]])],"derivedFrom":subQ0}),1.0]])]});}
            var Q65;
            {var subQ0=sQuery(id+"F0.wireOp",EDGE,"E22");var subQ1=makeQuery(id+"F0.imprint","INTERSECT",VERTEX,{"derivedFrom":[sQuery(id+"F0.wireOp",EDGE,"E19"),subQ0]});Q65=makeQuery(id+"F0.imprint","IMPRINT",FACE,{"disambiguationData":[TD([[makeQuery(id+"F0.imprint","IMPRINT",EDGE,{"disambiguationData":[TD([[subQ1,-1.0]])],"derivedFrom":subQ0}),1.0]])]});}
            var Q66;
            {var subQ0=sQuery(id+"F0.wireOp",EDGE,"E23");var subQ1=makeQuery(id+"F0.imprint","INTERSECT",VERTEX,{"derivedFrom":[sQuery(id+"F0.wireOp",EDGE,"E22"),subQ0]});Q66=makeQuery(id+"F0.imprint","IMPRINT",FACE,{"disambiguationData":[TD([[makeQuery(id+"F0.imprint","IMPRINT",EDGE,{"disambiguationData":[TD([[subQ1,-1.0]])],"derivedFrom":subQ0}),1.0]])]});}
            var Q67;
            {var subQ0=sQuery(id+"F0.wireOp",EDGE,"E30");var subQ1=makeQuery(id+"F0.imprint","INTERSECT",VERTEX,{"derivedFrom":[sQuery(id+"F0.wireOp",EDGE,"E27"),subQ0]});Q67=makeQuery(id+"F0.imprint","IMPRINT",FACE,{"disambiguationData":[TD([[makeQuery(id+"F0.imprint","IMPRINT",EDGE,{"disambiguationData":[TD([[subQ1,-1.0]])],"derivedFrom":subQ0}),1.0]])]});}
            var Q68;
            {var subQ0=sQuery(id+"F0.wireOp",EDGE,"E31");var subQ1=makeQuery(id+"F0.imprint","INTERSECT",VERTEX,{"derivedFrom":[sQuery(id+"F0.wireOp",EDGE,"E30"),subQ0]});Q68=makeQuery(id+"F0.imprint","IMPRINT",FACE,{"disambiguationData":[TD([[makeQuery(id+"F0.imprint","IMPRINT",EDGE,{"disambiguationData":[TD([[subQ1,-1.0]])],"derivedFrom":subQ0}),1.0]])]});}
            var Q69;
            {var subQ0=sQuery(id+"F0.wireOp",EDGE,"E38");var subQ1=makeQuery(id+"F0.imprint","INTERSECT",VERTEX,{"derivedFrom":[sQuery(id+"F0.wireOp",EDGE,"E35"),subQ0]});Q69=makeQuery(id+"F0.imprint","IMPRINT",FACE,{"disambiguationData":[TD([[makeQuery(id+"F0.imprint","IMPRINT",EDGE,{"disambiguationData":[TD([[subQ1,-1.0]])],"derivedFrom":subQ0}),1.0]])]});}
            var Q70;
            {var subQ0=sQuery(id+"F0.wireOp",EDGE,"E39");var subQ1=makeQuery(id+"F0.imprint","INTERSECT",VERTEX,{"derivedFrom":[sQuery(id+"F0.wireOp",EDGE,"E38"),subQ0]});Q70=makeQuery(id+"F0.imprint","IMPRINT",FACE,{"disambiguationData":[TD([[makeQuery(id+"F0.imprint","IMPRINT",EDGE,{"disambiguationData":[TD([[subQ1,-1.0]])],"derivedFrom":subQ0}),1.0]])]});}
            var Q71;
            {var subQ0=sQuery(id+"F0.wireOp",EDGE,"E63");var subQ1=makeQuery(id+"F0.imprint","INTERSECT",VERTEX,{"derivedFrom":[subQ0,sQuery(id+"F0.wireOp",EDGE,"E64")]});Q71=makeQuery(id+"F0.imprint","IMPRINT",FACE,{"disambiguationData":[TD([[makeQuery(id+"F0.imprint","IMPRINT",EDGE,{"disambiguationData":[TD([[subQ1,1.0]])],"derivedFrom":subQ0}),1.0]])]});}
            var Q72;
            {var subQ0=sQuery(id+"F0.wireOp",EDGE,"E27");var subQ1=makeQuery(id+"F0.imprint","INTERSECT",VERTEX,{"derivedFrom":[sQuery(id+"F0.wireOp",EDGE,"E24"),subQ0]});Q72=makeQuery(id+"F0.imprint","IMPRINT",FACE,{"disambiguationData":[TD([[makeQuery(id+"F0.imprint","IMPRINT",EDGE,{"disambiguationData":[TD([[subQ1,-1.0]])],"derivedFrom":subQ0}),1.0]])]});}
            var Q73;
            {var subQ0=sQuery(id+"F0.wireOp",EDGE,"E78");var subQ1=makeQuery(id+"F0.imprint","INTERSECT",VERTEX,{"derivedFrom":[sQuery(id+"F0.wireOp",EDGE,"E75"),subQ0]});Q73=makeQuery(id+"F0.imprint","IMPRINT",FACE,{"disambiguationData":[TD([[makeQuery(id+"F0.imprint","IMPRINT",EDGE,{"disambiguationData":[TD([[subQ1,-1.0]])],"derivedFrom":subQ0}),1.0]])]});}
            var Q74;
            {var subQ0=sQuery(id+"F0.wireOp",EDGE,"E83");var subQ1=makeQuery(id+"F0.imprint","INTERSECT",VERTEX,{"derivedFrom":[sQuery(id+"F0.wireOp",EDGE,"E81"),subQ0]});Q74=makeQuery(id+"F0.imprint","IMPRINT",FACE,{"disambiguationData":[TD([[makeQuery(id+"F0.imprint","IMPRINT",EDGE,{"disambiguationData":[TD([[subQ1,1.0]])],"derivedFrom":subQ0}),1.0]])]});}
            var Q75;
            {var subQ0=sQuery(id+"F0.wireOp",EDGE,"E20");var subQ1=makeQuery(id+"F0.imprint","INTERSECT",VERTEX,{"derivedFrom":[sQuery(id+"F0.wireOp",EDGE,"E19"),subQ0]});Q75=makeQuery(id+"F0.imprint","IMPRINT",FACE,{"disambiguationData":[TD([[makeQuery(id+"F0.imprint","IMPRINT",EDGE,{"disambiguationData":[TD([[subQ1,1.0]])],"derivedFrom":subQ0}),1.0]])]});}
            var Q76;
            {var subQ0=sQuery(id+"F0.wireOp",EDGE,"E64");var subQ1=makeQuery(id+"F0.imprint","INTERSECT",VERTEX,{"derivedFrom":[sQuery(id+"F0.wireOp",EDGE,"E63"),subQ0]});Q76=makeQuery(id+"F0.imprint","IMPRINT",FACE,{"disambiguationData":[TD([[makeQuery(id+"F0.imprint","IMPRINT",EDGE,{"disambiguationData":[TD([[subQ1,-1.0]])],"derivedFrom":subQ0}),1.0]])]});}
            var Q77;
            {var subQ0=sQuery(id+"F0.wireOp",EDGE,"E29");var subQ1=makeQuery(id+"F0.imprint","INTERSECT",VERTEX,{"derivedFrom":[sQuery(id+"F0.wireOp",EDGE,"E26"),subQ0]});Q77=makeQuery(id+"F0.imprint","IMPRINT",FACE,{"disambiguationData":[TD([[makeQuery(id+"F0.imprint","IMPRINT",EDGE,{"disambiguationData":[TD([[subQ1,-1.0]])],"derivedFrom":subQ0}),1.0]])]});}
            var Q78;
            {var subQ0=sQuery(id+"F0.wireOp",EDGE,"E80");var subQ1=makeQuery(id+"F0.imprint","INTERSECT",VERTEX,{"derivedFrom":[sQuery(id+"F0.wireOp",EDGE,"E53"),subQ0]});Q78=makeQuery(id+"F0.imprint","IMPRINT",FACE,{"disambiguationData":[TD([[makeQuery(id+"F0.imprint","IMPRINT",EDGE,{"disambiguationData":[TD([[subQ1,1.0]])],"derivedFrom":subQ0}),1.0]])]});}
            var Q79;
            {var subQ0=sQuery(id+"F0.wireOp",EDGE,"E25");var subQ1=makeQuery(id+"F0.imprint","INTERSECT",VERTEX,{"derivedFrom":[sQuery(id+"F0.wireOp",EDGE,"E20"),subQ0]});Q79=makeQuery(id+"F0.imprint","IMPRINT",FACE,{"disambiguationData":[TD([[makeQuery(id+"F0.imprint","IMPRINT",EDGE,{"disambiguationData":[TD([[subQ1,-1.0]])],"derivedFrom":subQ0}),1.0]])]});}
            var Q80;
            {var subQ0=sQuery(id+"F0.wireOp",EDGE,"E66");var subQ1=makeQuery(id+"F0.imprint","INTERSECT",VERTEX,{"derivedFrom":[sQuery(id+"F0.wireOp",EDGE,"E62"),subQ0]});Q80=makeQuery(id+"F0.imprint","IMPRINT",FACE,{"disambiguationData":[TD([[makeQuery(id+"F0.imprint","IMPRINT",EDGE,{"disambiguationData":[TD([[subQ1,-1.0]])],"derivedFrom":subQ0}),1.0]])]});}
            var Q81;
            {var subQ0=sQuery(id+"F0.wireOp",EDGE,"E9");var subQ1=makeQuery(id+"F0.imprint","INTERSECT",VERTEX,{"derivedFrom":[sQuery(id+"F0.wireOp",EDGE,"E0"),subQ0]});Q81=makeQuery(id+"F0.imprint","IMPRINT",FACE,{"disambiguationData":[TD([[makeQuery(id+"F0.imprint","IMPRINT",EDGE,{"disambiguationData":[TD([[subQ1,-1.0]])],"derivedFrom":subQ0}),1.0]])]});}
            var Q82;
            {var subQ0=sQuery(id+"F0.wireOp",EDGE,"E32");var subQ1=makeQuery(id+"F0.imprint","INTERSECT",VERTEX,{"derivedFrom":[sQuery(id+"F0.wireOp",EDGE,"E31"),subQ0]});Q82=makeQuery(id+"F0.imprint","IMPRINT",FACE,{"disambiguationData":[TD([[makeQuery(id+"F0.imprint","IMPRINT",EDGE,{"disambiguationData":[TD([[subQ1,1.0]])],"derivedFrom":subQ0}),1.0]])]});}
            var Q83;
            {var subQ0=sQuery(id+"F0.wireOp",EDGE,"E84");var subQ1=makeQuery(id+"F0.imprint","INTERSECT",VERTEX,{"derivedFrom":[sQuery(id+"F0.wireOp",EDGE,"E6"),subQ0]});Q83=makeQuery(id+"F0.imprint","IMPRINT",FACE,{"disambiguationData":[TD([[makeQuery(id+"F0.imprint","IMPRINT",EDGE,{"disambiguationData":[TD([[subQ1,-1.0]])],"derivedFrom":subQ0}),1.0]])]});}
            var Q84;
            {var subQ0=sQuery(id+"F0.wireOp",EDGE,"E54");var subQ1=makeQuery(id+"F0.imprint","INTERSECT",VERTEX,{"derivedFrom":[sQuery(id+"F0.wireOp",EDGE,"E51"),subQ0]});Q84=makeQuery(id+"F0.imprint","IMPRINT",FACE,{"disambiguationData":[TD([[makeQuery(id+"F0.imprint","IMPRINT",EDGE,{"disambiguationData":[TD([[subQ1,1.0]])],"derivedFrom":subQ0}),1.0]])]});}
            var Q85;
            {var subQ0=sQuery(id+"F0.wireOp",EDGE,"E79");var subQ1=makeQuery(id+"F0.imprint","INTERSECT",VERTEX,{"derivedFrom":[sQuery(id+"F0.wireOp",EDGE,"E54"),subQ0]});Q85=makeQuery(id+"F0.imprint","IMPRINT",FACE,{"disambiguationData":[TD([[makeQuery(id+"F0.imprint","IMPRINT",EDGE,{"disambiguationData":[TD([[subQ1,1.0]])],"derivedFrom":subQ0}),1.0]])]});}
            var Q86;
            {var subQ0=sQuery(id+"F0.wireOp",EDGE,"E28");var subQ1=makeQuery(id+"F0.imprint","INTERSECT",VERTEX,{"derivedFrom":[sQuery(id+"F0.wireOp",EDGE,"E27"),subQ0]});Q86=makeQuery(id+"F0.imprint","IMPRINT",FACE,{"disambiguationData":[TD([[makeQuery(id+"F0.imprint","IMPRINT",EDGE,{"disambiguationData":[TD([[subQ1,1.0]])],"derivedFrom":subQ0}),1.0]])]});}
            var Q87;
            {var subQ0=sQuery(id+"F0.wireOp",EDGE,"E44");var subQ1=makeQuery(id+"F0.imprint","INTERSECT",VERTEX,{"derivedFrom":[sQuery(id+"F0.wireOp",EDGE,"E43"),subQ0]});Q87=makeQuery(id+"F0.imprint","IMPRINT",FACE,{"disambiguationData":[TD([[makeQuery(id+"F0.imprint","IMPRINT",EDGE,{"disambiguationData":[TD([[subQ1,1.0]])],"derivedFrom":subQ0}),1.0]])]});}
            extrude(context, id + "F1", {"entities" : qUnion([Q0, Q1, Q2, Q3, Q4, Q5, Q6, Q7, Q8, Q9, Q10, Q11, Q12, Q13, Q14, Q15, Q16, Q17, Q18, Q19, Q20, Q21, Q22, Q23, Q24, Q25, Q26, Q27, Q28, Q29, Q30, Q31, Q32, Q33, Q34, Q35, Q36, Q37, Q38, Q39, Q40, Q41, Q42, Q43, Q44, Q45, Q46, Q47, Q48, Q49, Q50, Q51, Q52, Q53, Q54, Q55, Q56, Q57, Q58, Q59, Q60, Q61, Q62, Q63, Q64, Q65, Q66, Q67, Q68, Q69, Q70, Q71, Q72, Q73, Q74, Q75, Q76, Q77, Q78, Q79, Q80, Q81, Q82, Q83, Q84, Q85, Q86, Q87]), "depth" : 78.46 * mm});
        }
    });
